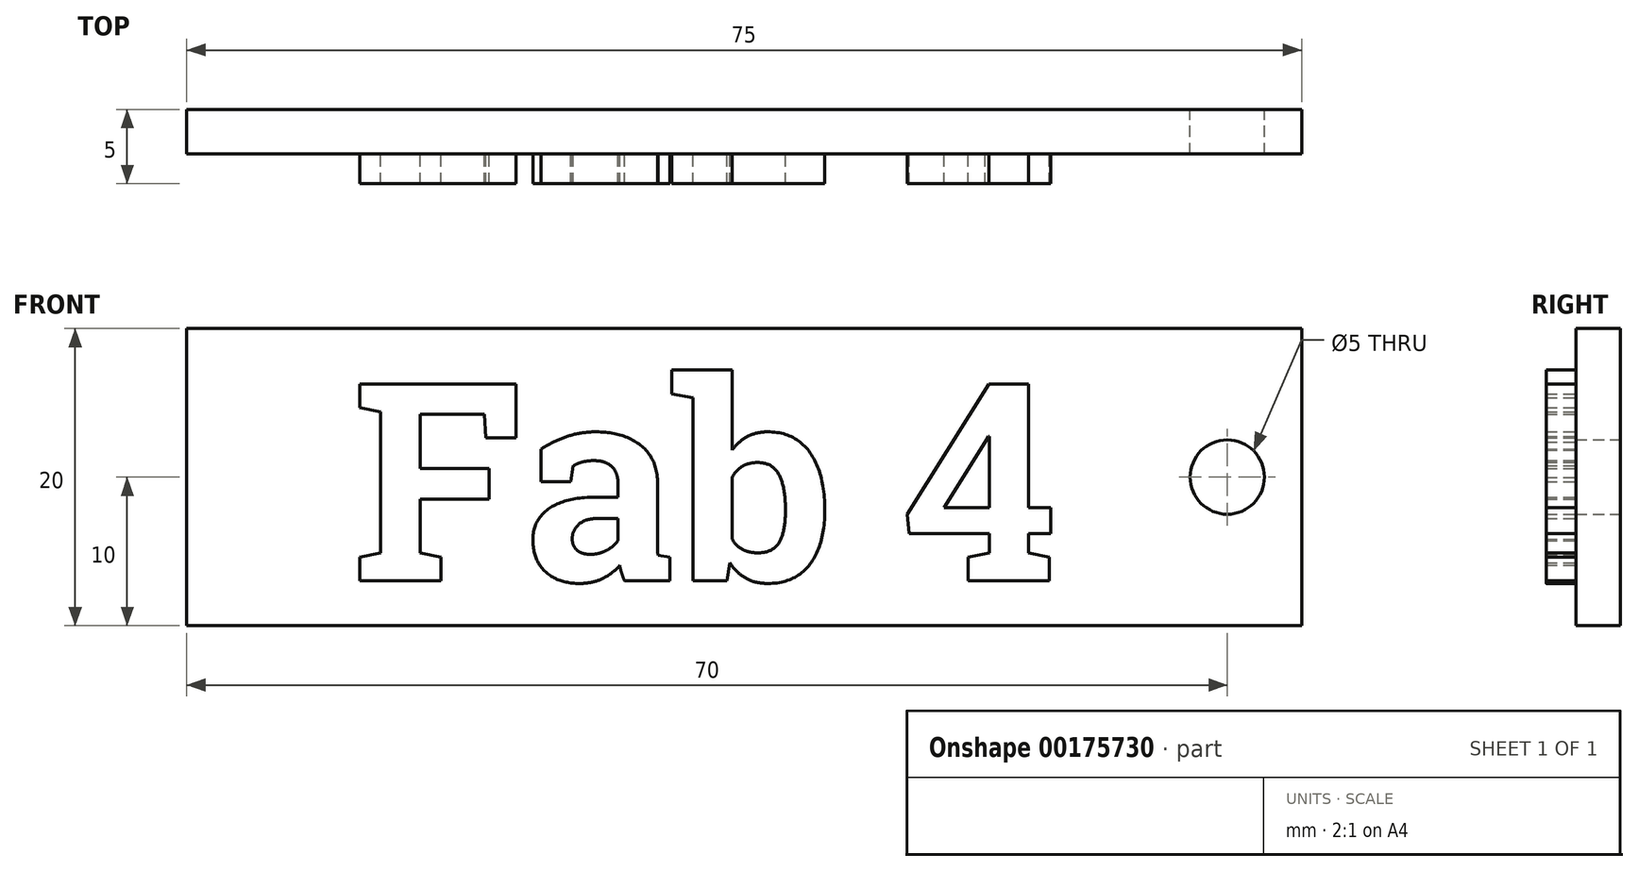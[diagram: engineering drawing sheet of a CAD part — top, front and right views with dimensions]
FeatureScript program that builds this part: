
annotation { "Feature Type Name" : "Feature", "Feature Type Description" : "" }
export const myFeature = defineFeature(function(context is Context, id is Id, definition is map)
    precondition{}
    {
        {
            var Q0;
            Q0=qCreatedBy(makeId("Front.planeOp"),FACE);
            var sketch = newSketch(context, id + "F0", { "sketchPlane" : qUnion([Q0])});
            skLineSegment(sketch, "E0.bottom", {"start": v(0, 0) * mm, "end": v(75, 0) * mm});
            skLineSegment(sketch, "E0.top", {"start": v(0, -20) * mm, "end": v(75, -20) * mm});
            skLineSegment(sketch, "E0.left", {"start": v(0, 0) * mm, "end": v(0, -20) * mm});
            skLineSegment(sketch, "E0.right", {"start": v(75, 0) * mm, "end": v(75, -20) * mm});
            skCircle(sketch, "E1", {"center": v(70, -10) * mm, "radius": 2.5 * mm});
            skSolve(sketch);
        }
        {
            var Q0;
            Q0=makeQuery(id+"F0.imprint","IMPRINT",FACE,{"disambiguationData":[TD([[makeQuery(id+"F0.imprint","IMPRINT",EDGE,{"derivedFrom":sQuery(id+"F0.wireOp",EDGE,"E0.bottom")}),-1.0]])]});
            extrude(context, id + "F1", {"entities" : qUnion([Q0]), "depth" : 3 * mm});
        }
        {
            var Q0;
            Q0=makeQuery(id+"F1.opExtrude","CAP_FACE",FACE,{"disambiguationData":[OSD([sQuery(id+"F0.wireOp",EDGE,"E0.bottom"),sQuery(id+"F0.wireOp",EDGE,"E0.top"),sQuery(id+"F0.wireOp",EDGE,"E0.left"),sQuery(id+"F0.wireOp",EDGE,"E0.right"),sQuery(id+"F0.wireOp",EDGE,"E1")])],"isStart":false});
            var sketch = newSketch(context, id + "F2", { "sketchPlane" : qUnion([Q0])});
            skText(sketch, "E2", { "text": "Fab 4", "fontName": "RobotoSlab-Bold.ttf"});
            const initialGuessF2  = {"E2": [0.01112, -0.01697, 1, 0, 0.0134]};
            skSetInitialGuess(sketch, initialGuessF2);
            skSolve(sketch);
        }
        {
            var Q0;
            Q0 = qSketchRegion(id + "F2", true);
            extrude(context, id + "F3", {"entities" : qUnion([Q0]), "operationType" : NewBodyOperationType.ADD, "depth" : 2 * mm});
        }
        {
            var Q0;
            Q0 = qSketchRegion(id + "F2", true);
            extrude(context, id + "F4", {"entities" : qUnion([Q0]), "operationType" : NewBodyOperationType.ADD, "depth" : 2 * mm});
        }
        {
            var Q0;
            Q0 = qSketchRegion(id + "F2", true);
            extrude(context, id + "F5", {"entities" : qUnion([Q0]), "operationType" : NewBodyOperationType.ADD, "depth" : 2 * mm});
        }
    });
